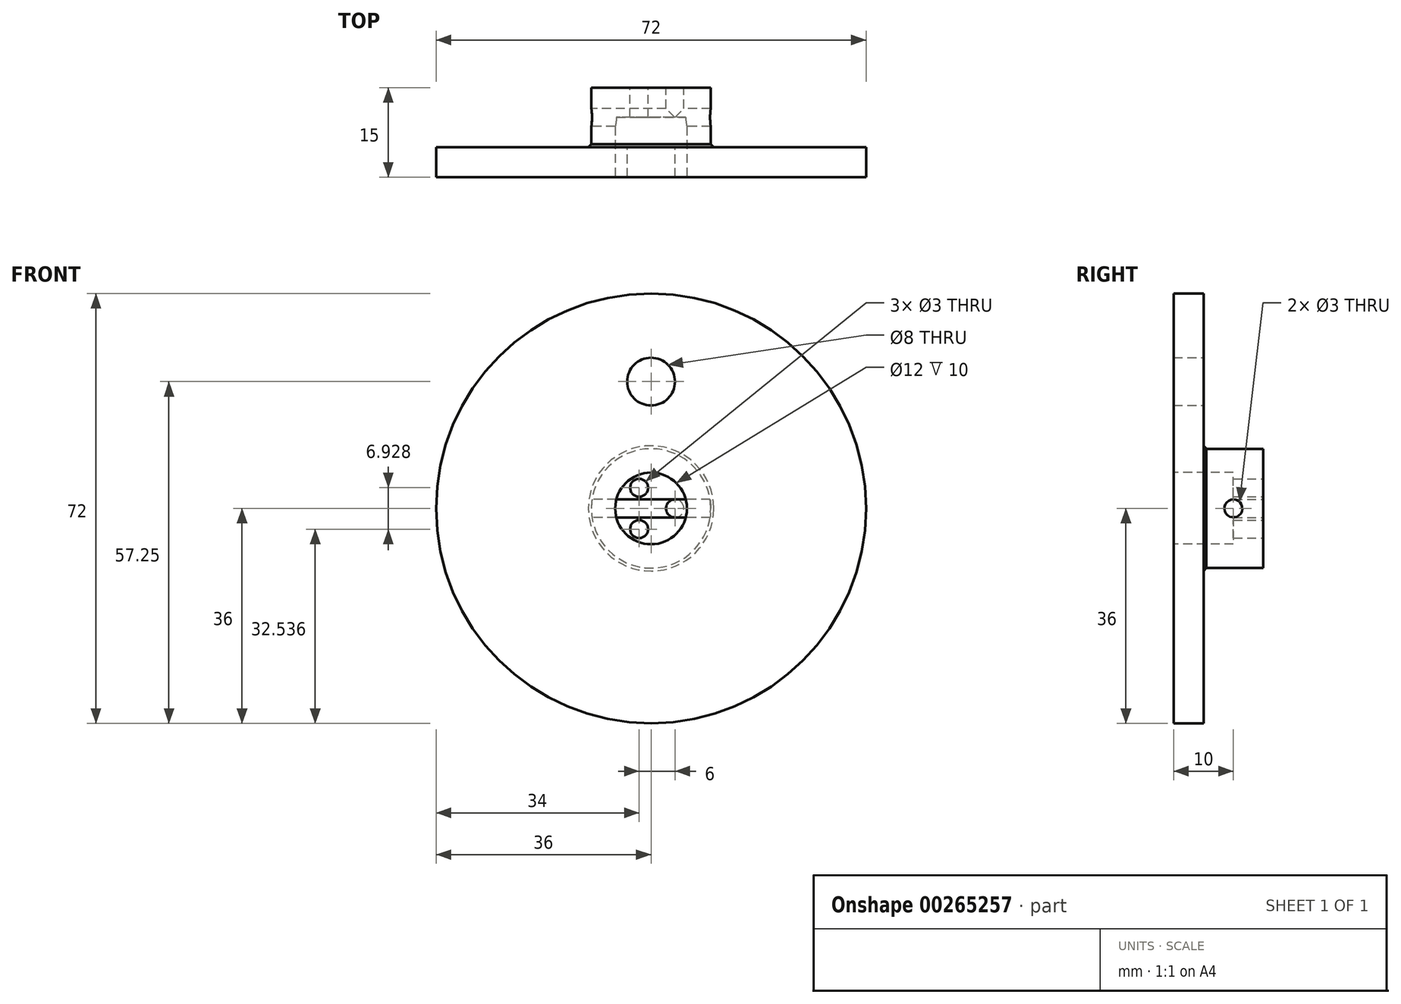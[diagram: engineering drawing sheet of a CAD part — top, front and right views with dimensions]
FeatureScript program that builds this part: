
annotation { "Feature Type Name" : "Feature", "Feature Type Description" : "" }
export const myFeature = defineFeature(function(context is Context, id is Id, definition is map)
    precondition{}
    {
        {
            var Q0;
            Q0=qCreatedBy(makeId("Front.planeOp"),FACE);
            var sketch = newSketch(context, id + "F0", { "sketchPlane" : qUnion([Q0])});
            skCircle(sketch, "E0", {"center": v(0, 0) * mm, "radius": 36 * mm});
            skSolve(sketch);
        }
        {
            var Q0;
            Q0=makeQuery(id+"F0.imprint","IMPRINT",FACE,{"disambiguationData":[TD([[makeQuery(id+"F0.imprint","IMPRINT",EDGE,{"derivedFrom":sQuery(id+"F0.wireOp",EDGE,"E0")}),1.0]])]});
            extrude(context, id + "F1", {"entities" : qUnion([Q0]), "depth" : 15 * mm});
        }
        {
            var Q0;
            Q0=makeQuery(id+"F1.opExtrude","CAP_FACE",FACE,{"disambiguationData":[OSD([sQuery(id+"F0.wireOp",EDGE,"E0")])],"isStart":true});
            var sketch = newSketch(context, id + "F2", { "sketchPlane" : qUnion([Q0])});
            skCircle(sketch, "E1", {"center": v(0, 0) * mm, "radius": 10 * mm});
            skCircle(sketch, "E2", {"center": v(0, 0) * mm, "radius": 65 * mm});
            skSolve(sketch);
        }
        {
            var Q0;
            Q0=qSketchRegion(id+"F2",true);
            extrude(context, id + "F3", {"entities" : qUnion([Q0]), "operationType" : NewBodyOperationType.REMOVE, "oppositeDirection" : true, "depth" : 10 * mm});
        }
        {
            var Q0;
            Q0=makeQuery(id+"F3.boolean.opBoolean","COPY",EDGE,{"derivedFrom":makeQuery(id+"F3.opExtrude","CAP_EDGE",EDGE,{"disambiguationData":[OSD([sQuery(id+"F2.wireOp",EDGE,"E1")])],"isStart":false})});
            chamfer(context, id + "F4", {"entities" : qUnion([Q0]), "width" : .5 * mm, "tangentPropagation" : true});
        }
        {
            var Q0;
            Q0=qCreatedBy(makeId("Right.planeOp"),FACE);
            var sketch = newSketch(context, id + "F5", { "sketchPlane" : qUnion([Q0])});
            skPoint(sketch, "E3", {"position": v(-5, 0) * mm});
            skCircle(sketch, "E4", {"center": v(-5, 0) * mm, "radius": 1.5 * mm});
            skSolve(sketch);
        }
        {
            var Q0;
            Q0=qSketchRegion(id+"F5",true);
            extrude(context, id + "F6", {"entities" : qUnion([Q0]), "operationType" : NewBodyOperationType.REMOVE, "depth" : 25 * mm, "hasSecondDirection" : true, "secondDirectionOppositeDirection" : true, "secondDirectionDepth" : 25 * mm});
        }
        {
            var Q0;
            Q0=qCreatedBy(makeId("Front.planeOp"),FACE);
            var sketch = newSketch(context, id + "F7", { "sketchPlane" : qUnion([Q0])});
            skPoint(sketch, "E5", {"position": v(0, 0) * mm});
            skPoint(sketch, "E6", {"position": v(0, 21.25) * mm});
            skCircle(sketch, "E7", {"center": v(0, 21.25) * mm, "radius": 4 * mm});
            skSolve(sketch);
        }
        {
            var Q0;
            Q0=qSketchRegion(id+"F7",true);
            extrude(context, id + "F8", {"entities" : qUnion([Q0]), "operationType" : NewBodyOperationType.REMOVE, "depth" : 25 * mm});
        }
        {
            var Q0;
            Q0=qCreatedBy(makeId("Front.planeOp"),FACE);
            var sketch = newSketch(context, id + "F9", { "sketchPlane" : qUnion([Q0])});
            skCircle(sketch, "E8.cCircle", {"center": v(0, 0) * mm, "radius": 2 * mm, "construction": true});
            skLineSegment(sketch, "E8.0", {"start": v(-2, -3.46) * mm, "end": v(-2, 3.46) * mm, "construction": true});
            skLineSegment(sketch, "E8.1", {"start": v(-2, 3.46) * mm, "end": v(4, 0) * mm, "construction": true});
            skLineSegment(sketch, "E8.2", {"start": v(4, 0) * mm, "end": v(-2, -3.46) * mm, "construction": true});
            skPoint(sketch, "E8.0.midPoint", {"position": v(-2, 0) * mm});
            skCircle(sketch, "E9", {"center": v(-2, 3.46) * mm, "radius": 1.5 * mm});
            skCircle(sketch, "E10", {"center": v(-2, -3.46) * mm, "radius": 1.5 * mm});
            skCircle(sketch, "E11", {"center": v(4, 0) * mm, "radius": 1.5 * mm});
            skSolve(sketch);
        }
        {
            var Q0;
            Q0=qSketchRegion(id+"F9",true);
            extrude(context, id + "F10", {"entities" : qUnion([Q0]), "operationType" : NewBodyOperationType.REMOVE, "depth" : 15 * mm});
        }
        {
            var Q0;
            Q0=makeQuery(id+"F1.opExtrude","CAP_FACE",FACE,{"disambiguationData":[OSD([sQuery(id+"F0.wireOp",EDGE,"E0")])],"isStart":false});
            var sketch = newSketch(context, id + "F11", { "sketchPlane" : qUnion([Q0])});
            skPoint(sketch, "E12", {"position": v(0, 0) * mm});
            skCircle(sketch, "E13", {"center": v(0, 0) * mm, "radius": 6 * mm});
            skSolve(sketch);
        }
        {
            var Q0;
            Q0 = qSketchRegion(id + "F11", true);
            extrude(context, id + "F12", {"entities" : qUnion([Q0]), "operationType" : NewBodyOperationType.REMOVE, "oppositeDirection" : true, "depth" : 10 * mm});
        }
    });
